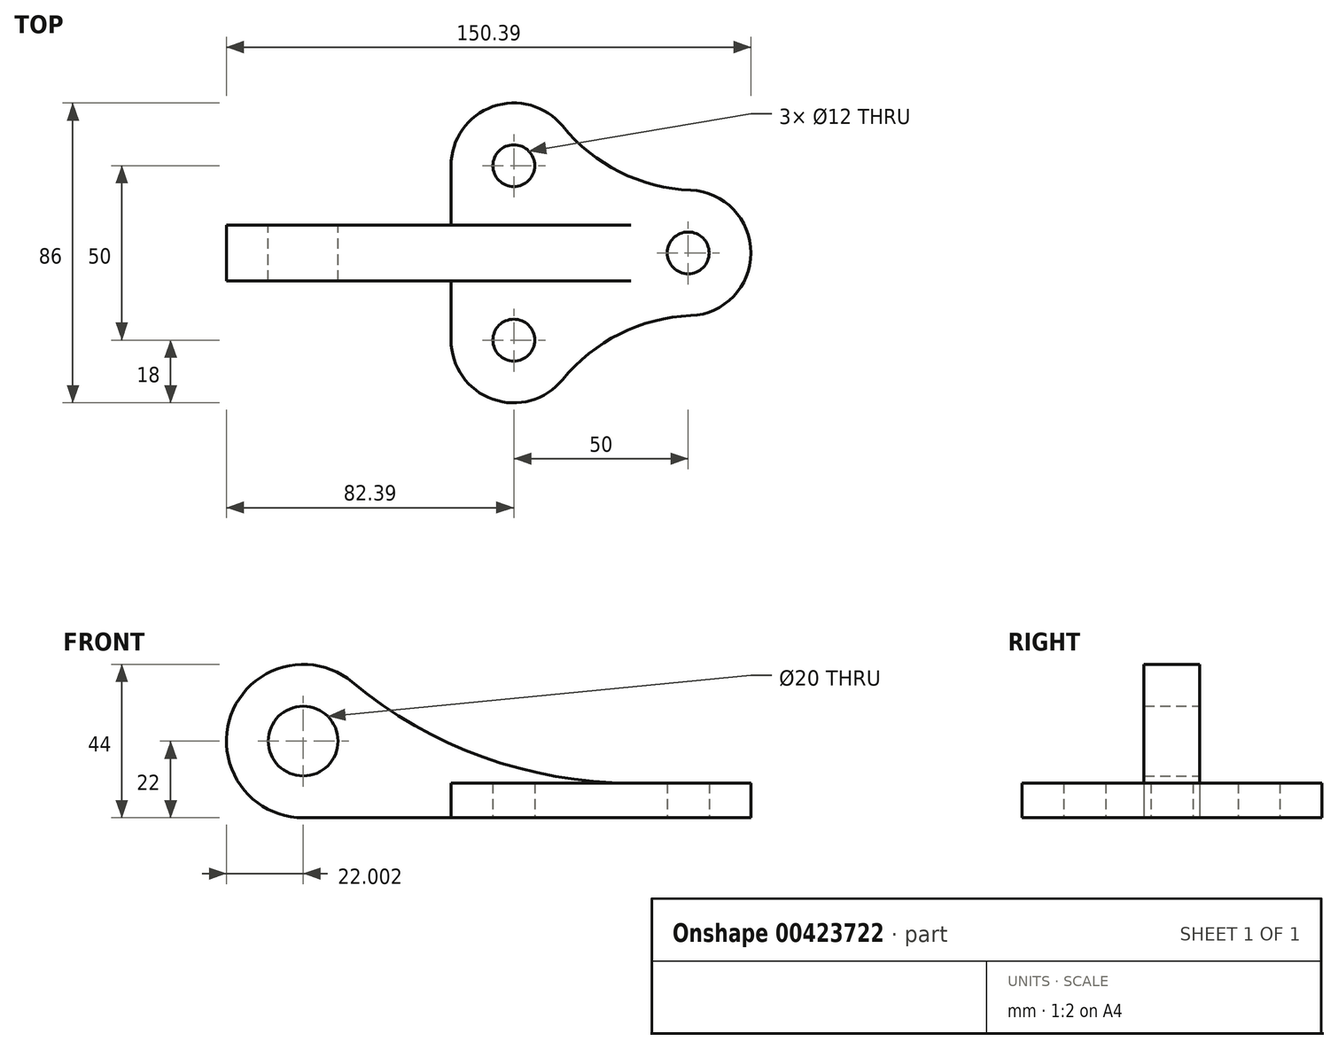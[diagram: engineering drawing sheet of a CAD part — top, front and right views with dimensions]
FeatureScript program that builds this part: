
annotation { "Feature Type Name" : "Feature", "Feature Type Description" : "" }
export const myFeature = defineFeature(function(context is Context, id is Id, definition is map)
    precondition{}
    {
        {
            var Q0;
            Q0=qCreatedBy(makeId("Top.planeOp"),FACE);
            var sketch = newSketch(context, id + "F0", { "sketchPlane" : qUnion([Q0])});
            skArc(sketch, "E0", {"start": v(13.96, 36.37) * mm, "mid": v(-6.03, 41.96) * mm, "end": v(-18, 25) * mm});
            skCircle(sketch, "E1", {"center": v(0, 25) * mm, "radius": 6 * mm});
            skArc(sketch, "E2.MirrorC", {"start": v(13.96, -36.37) * mm, "mid": v(-6.03, -41.96) * mm, "end": v(-18, -25) * mm});
            skCircle(sketch, "E3.MirrorC", {"center": v(0, -25) * mm, "radius": 6 * mm});
            skArc(sketch, "E4", {"start": v(50.72, -17.99) * mm, "mid": v(68, 0) * mm, "end": v(50.72, 17.99) * mm});
            skCircle(sketch, "E5", {"center": v(50, 0) * mm, "radius": 6 * mm});
            skArc(sketch, "E6", {"start": v(50.72, -17.99) * mm, "mid": v(30.36, -23.22) * mm, "end": v(13.96, -36.37) * mm});
            skPoint(sketch, "E6.first.point", {"position": v(50.72, -17.99) * mm});
            skPoint(sketch, "E6.second.point", {"position": v(13.96, -36.37) * mm});
            skPoint(sketch, "E6.third.point", {"position": v(100.96, -81.1) * mm});
            skArc(sketch, "E7.MirrorC", {"start": v(50.72, 17.99) * mm, "mid": v(30.36, 23.22) * mm, "end": v(13.96, 36.37) * mm});
            skLineSegment(sketch, "E8", {"start": v(-18, 25) * mm, "end": v(-18, -25) * mm});
            skSolve(sketch);
        }
        {
            var Q0;
            Q0 = qSketchRegion(id + "F0", true);
            extrude(context, id + "F1", {"entities" : qUnion([Q0]), "depth" : 10 * mm});
        }
        {
            var Q0;
            Q0=qCreatedBy(makeId("Front.planeOp"),FACE);
            var sketch = newSketch(context, id + "F2", { "sketchPlane" : qUnion([Q0])});
            skArc(sketch, "E9", {"start": v(-46.32, 38.91) * mm, "mid": v(-81.08, 29.48) * mm, "end": v(-60.39, 0) * mm});
            skCircle(sketch, "E10", {"center": v(-60.39, 22) * mm, "radius": 10 * mm});
            skLineSegment(sketch, "E11", {"start": v(-60.39, 0) * mm, "end": v(33.63, 0) * mm});
            skArc(sketch, "E12", {"start": v(-46.32, 38.91) * mm, "mid": v(-8.88, 17.45) * mm, "end": v(33.63, 10) * mm});
            skLineSegment(sketch, "E13", {"start": v(33.63, 10) * mm, "end": v(33.63, 0) * mm});
            skPoint(sketch, "E14.orphan", {"position": v(49.61, 0) * mm});
            skSolve(sketch);
        }
        {
            var Q0;
            Q0 = qSketchRegion(id + "F2", true);
            extrude(context, id + "F3", {"entities" : qUnion([Q0]), "operationType" : NewBodyOperationType.ADD, "depth" : 8 * mm, "hasSecondDirection" : true, "secondDirectionOppositeDirection" : true, "secondDirectionDepth" : 8 * mm});
        }
    });
